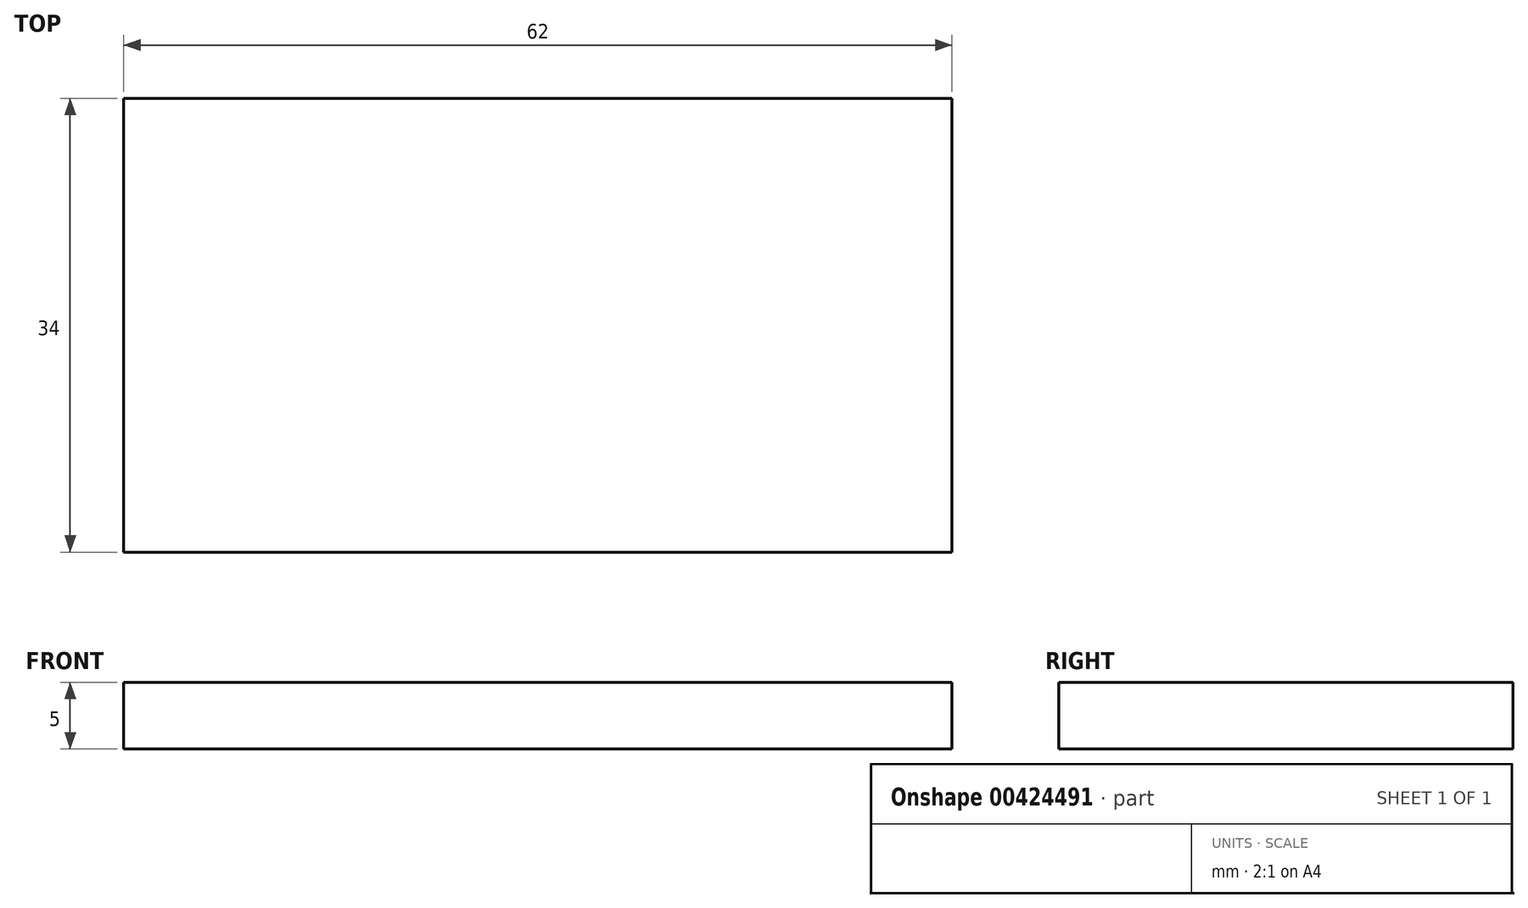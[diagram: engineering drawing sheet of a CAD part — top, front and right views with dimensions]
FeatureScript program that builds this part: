
annotation { "Feature Type Name" : "Feature", "Feature Type Description" : "" }
export const myFeature = defineFeature(function(context is Context, id is Id, definition is map)
    precondition{}
    {
        {
            var Q0;
            Q0=qCreatedBy(makeId("Top.planeOp"),FACE);
            var sketch = newSketch(context, id + "F0", { "sketchPlane" : qUnion([Q0])});
            skLineSegment(sketch, "E0.bottom", {"start": v(31, 17) * mm, "end": v(-31, 17) * mm});
            skLineSegment(sketch, "E0.top", {"start": v(31, -17) * mm, "end": v(-31, -17) * mm});
            skLineSegment(sketch, "E0.left", {"start": v(31, 17) * mm, "end": v(31, -17) * mm});
            skLineSegment(sketch, "E0.right", {"start": v(-31, 17) * mm, "end": v(-31, -17) * mm});
            skPoint(sketch, "E0.middle", {"position": v(0, 0) * mm});
            skSolve(sketch);
        }
        {
            var Q0;
            Q0=makeQuery(id+"F0.imprint","IMPRINT",FACE,{"disambiguationData":[TD([[makeQuery(id+"F0.imprint","IMPRINT",EDGE,{"derivedFrom":sQuery(id+"F0.wireOp",EDGE,"E0.bottom")}),1.0]])]});
            extrude(context, id + "F1", {"entities" : qUnion([Q0]), "depth" : 5 * mm});
        }
    });
